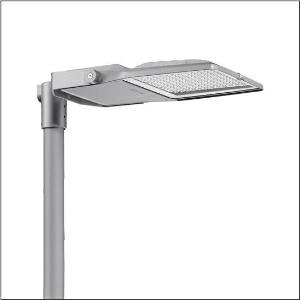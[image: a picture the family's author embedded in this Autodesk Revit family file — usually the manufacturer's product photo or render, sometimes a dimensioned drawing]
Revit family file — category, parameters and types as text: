
# Revit family: floodlight_fl_21_iq_midi___pl52_5xa7782e4d3a_8c54
name_source: partatom
category: Lighting Fixtures
units: mm (PartAtom-declared; Revit-internal decimal feet)

## family parameters
Cut with Voids When Loaded = No
Host = Face
Light Source = No
Part Type = Normal
Room Calculation Point = No
Round Connector Dimension = Use Diameter
Shared = No

## types (1)
- --- (1 x LED, 28010 lm, 208.1 W, 4000K)
    Apparent Load = 208 VA
    CIE Flux Codes = 26 60 98 100 100
    Color Rendering = 70
    Color Temperature = 4000K
    Default Elevation = 1800 mm
    Description = Floodlight FL 21 iQ midi, floodlight, primary light control with lens, of PMMA, primary optical cover: protective disc, of toughened safety glass, transparent, light distribution: PL52, light emission: direct distribution, installation type: surface-mounted, LED, High Power LED, rated luminous flux: 28.010lm, luminous efficacy: 135lm/W, light colour: 740, colour temperature: 4000K, control gear: ECG iQ, control: optimised constant luminous flux control (CLO 2.0), Desk-Remote (wireless, voltage-free reading and setting of iQ features in the workshop via application-optimized NFC function/RFID function), Smart-Wire, Night-Set, Temp-Guard, Auto-Match, Street-Remote, with terminal, 6-pole, mains connection: 220..240V, AC, 50/60Hz, start of lifetime: 208W, end of service life: 227W, reduction: 90W, luminaire housing, of diecast aluminium, powder-coated, Siteco® metallic grey (DB 702S), corrosivity category C5 mid according to DIN EN ISO 12944, sealing non-destructively replaceable, please order mast flange separately, mast bracket, of steel, galvanised, powder-coated, Siteco® metallic grey (DB 702S), protection rating (complete): IP66, insulation class (complete): insulation class II (safety insulation), certification: CE, ENEC, VDE, protection symbol: D, impact resistance: IK08, permissible operating ambient temperature: -40..+40°C, permissible operating ambient temperature for outdoor applications: -40..+50°C, standard: DIN EN 12944, LABS conformity tested according to VDMA 24364:2018-05, packaging unit: 1 piece

Light Distribution: PL52
    Height = 76 mm
    Lamp = 1 x LED
    Lamp Light Flux = 28010 lm
    Lamp Power = 208.1 W
    Lamp count = 1
    Length = 657 mm
    Luminous efficacy = 135 lm/W
    Manufacturer = Siteco
    ModVariant = No
    Model = 5XA7782E4D3A
    Number of Poles = 1
    OnlyDefault = Yes
    Power Factor = 1
    Product Name = Floodlight FL 21 iQ midi | PL52
    Product group = floodlight | pylon annexe
    ProductGroupID = 6200
    Protection Class = Protection class II
    Protection Degree = IP 66
    RLX_Detail_Level = 1
    RLX_Emergency_Light_Flux = 0 lm
    RLX_Emergency_Type = 0
    RLX_Emergency_Type_DB = No
    RlxData = <blob elided: 153661 chars, md5=e6c98caa>
    Socket = socket
    Standby Power = 0 W
    System Light Flux = 28010 lm
    System Power = 208 W
    Type Comments = factory setting: luminous flux: 100 % | dim-lin: 254 | 710 mA
    Type Image = l_1007123.jpg
    URL = http://relux.com
    VarID = @adj_074819
    Voltage = 0 V
    Weight = 0.00 kg
    Width = 442 mm

## geometry (parser evidence)
native form markers: Blend x4, Sweep x16
no freeform markers — native parametric forms only
